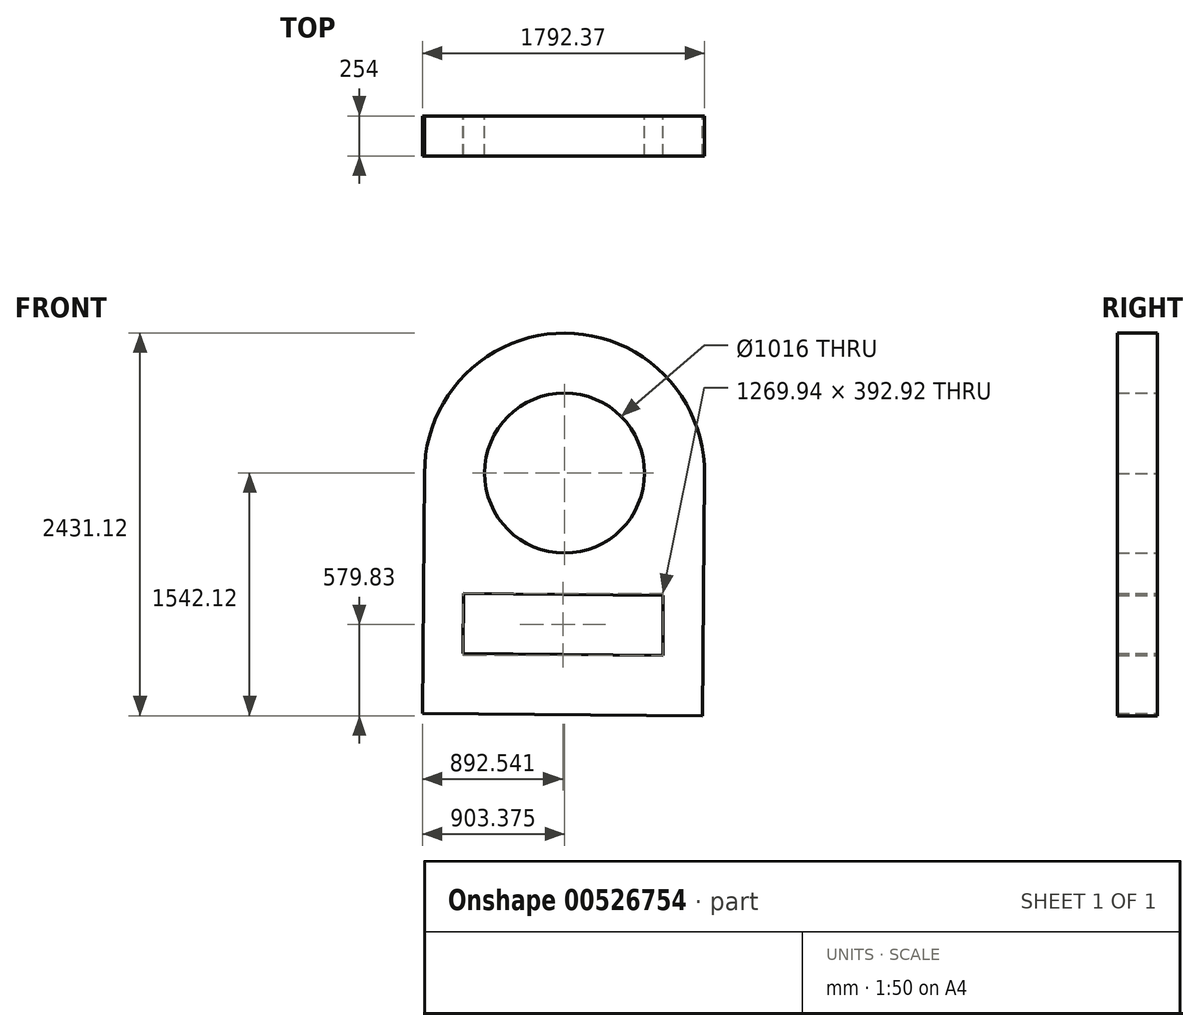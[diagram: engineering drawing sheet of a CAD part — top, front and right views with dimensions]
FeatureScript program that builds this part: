
annotation { "Feature Type Name" : "Feature", "Feature Type Description" : "" }
export const myFeature = defineFeature(function(context is Context, id is Id, definition is map)
    precondition{}
    {
        {
            var Q0;
            Q0=qCreatedBy(makeId("Front.planeOp"),FACE);
            var sketch = newSketch(context, id + "F0", { "sketchPlane" : qUnion([Q0])});
            skLineSegment(sketch, "E0", {"start": v(0, 0) * mm, "end": v(1777.92, -16.7) * mm});
            skLineSegment(sketch, "E1", {"start": v(1777.92, -16.7) * mm, "end": v(1792.24, 1507.22) * mm});
            skLineSegment(sketch, "E2", {"start": v(0, 0) * mm, "end": v(14.32, 1523.93) * mm});
            skLineSegment(sketch, "E3", {"start": v(261.15, 759.58) * mm, "end": v(257.57, 378.6) * mm});
            skLineSegment(sketch, "E4", {"start": v(257.57, 378.6) * mm, "end": v(1527.51, 366.66) * mm});
            skLineSegment(sketch, "E5", {"start": v(1527.51, 366.66) * mm, "end": v(1527.51, 747.66) * mm});
            skLineSegment(sketch, "E6", {"start": v(1527.51, 747.66) * mm, "end": v(261.15, 759.58) * mm});
            skArc(sketch, "E7", {"start": v(1792.34, 1517.06) * mm, "mid": v(906.81, 2414.4) * mm, "end": v(14.38, 1523.93) * mm});
            skLineSegment(sketch, "E8", {"start": v(1792.24, 1507.22) * mm, "end": v(1792.34, 1517.06) * mm});
            skPoint(sketch, "E9.end.orphan", {"position": v(0, 1902.44) * mm});
            skLineSegment(sketch, "E10", {"start": v(14.38, 1523.93) * mm, "end": v(14.32, 1523.93) * mm});
            skPoint(sketch, "E11.orphan", {"position": v(139.4, 1523.93) * mm});
            skPoint(sketch, "E12.start.orphan", {"position": v(0, 2051.59) * mm});
            skCircle(sketch, "E13", {"center": v(903.37, 1525.41) * mm, "radius": 508 * mm});
            skSolve(sketch);
        }
        {
            var Q0;
            Q0 = qSketchRegion(id + "F0", true);
            extrude(context, id + "F1", {"entities" : qUnion([Q0]), "depth" : 254 * mm, "offsetDistance" : 25.4 * mm});
        }
    });
